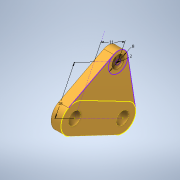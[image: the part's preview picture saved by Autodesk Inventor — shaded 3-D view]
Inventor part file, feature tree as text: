
AUTODESK INVENTOR PART (.ipt)
format: ipt  version: 2020 (Build 240168000, 168)  size: 149,504 bytes
history: native  units: in
note: dims shown in document units (in); Inventor stores cm internally (conversion verified against a paired STEP export)
features: extrude x3, sketch x3, projected_geometry x1
ambient origin geometry x8: Origin, YZ Plane, XZ Plane, XY Plane, X Axis, Y Axis, Z Axis, Center Point
bodies: Solid1 (feature_tree)
feature tree (7):
  extrude  "Extrusion1"  Depth=0.4523in
  extrude  "Extrusion2"  Depth=0.2118in
  extrude  "Extrusion3"  Depth=0.1575in TaperAngle=0.0deg
  sketch  "Sketch1"  dims[d0=0.2008in d1=0.2008in d3=0.4523in]
  sketch  "Sketch2"  dims[d4=0.2118in d5=0.8586in]
  projected_geometry  "Projected Loop1"
  sketch  "Sketch3"  dims[d6=0.8656in d7=0.1575in d8=0.0in d9=0.4331in d10=0.7087in d11=0.0787in d12=0.315in d13=0.1575in d14=0.0in d15=0.1969in d16=0.0787in d17=0.0in]
